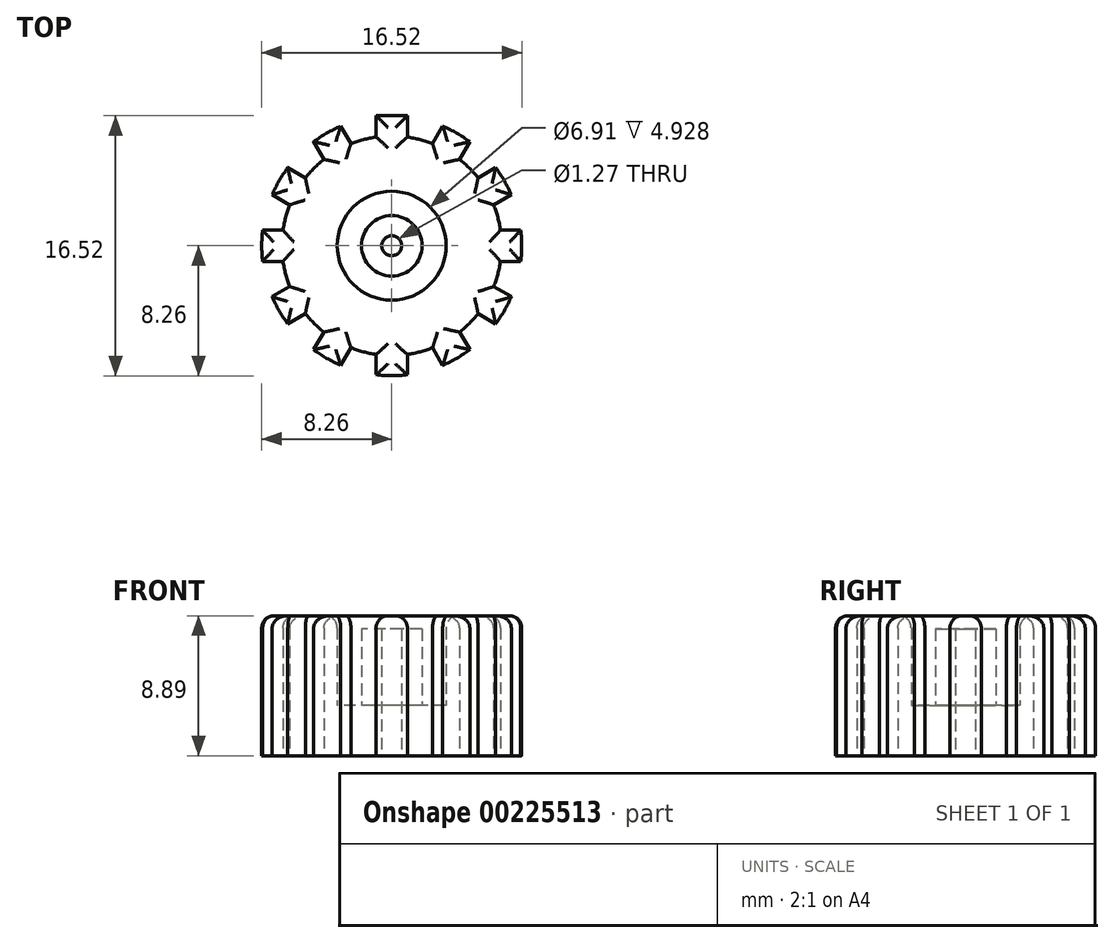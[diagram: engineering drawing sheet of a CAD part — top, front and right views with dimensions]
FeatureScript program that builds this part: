
annotation { "Feature Type Name" : "Feature", "Feature Type Description" : "" }
export const myFeature = defineFeature(function(context is Context, id is Id, definition is map)
    precondition{}
    {
        {
            var Q0;
            Q0=qCreatedBy(makeId("Top.planeOp"),FACE);
            var sketch = newSketch(context, id + "F0", { "sketchPlane" : qUnion([Q0])});
            skArc(sketch, "E0", {"start": v(-1, 8.2) * mm, "mid": v(0, -8.26) * mm, "end": v(1, 8.2) * mm});
            skCircle(sketch, "E1", {"center": v(0, 0) * mm, "radius": 0.64 * mm});
            skCircle(sketch, "E2", {"center": v(0, 0) * mm, "radius": 6.97 * mm});
            skLineSegment(sketch, "E3.top", {"start": v(-1, 8.26) * mm, "end": v(1, 8.26) * mm});
            skLineSegment(sketch, "E3.left", {"start": v(-1, 6.9) * mm, "end": v(-1, 8.26) * mm});
            skLineSegment(sketch, "E3.right", {"start": v(1, 6.9) * mm, "end": v(1, 8.26) * mm});
            skPoint(sketch, "E3.middle", {"position": v(0, 7.58) * mm});
            skLineSegment(sketch, "E4.1.0", {"start": v(-4.99, 6.65) * mm, "end": v(-3.27, 7.65) * mm});
            skLineSegment(sketch, "E4.1.1", {"start": v(-4.31, 5.48) * mm, "end": v(-4.99, 6.65) * mm});
            skLineSegment(sketch, "E4.1.2", {"start": v(-2.6, 6.47) * mm, "end": v(-3.27, 7.65) * mm});
            skLineSegment(sketch, "E4.2.0", {"start": v(-7.65, 3.27) * mm, "end": v(-6.65, 4.99) * mm});
            skLineSegment(sketch, "E4.2.1", {"start": v(-6.47, 2.6) * mm, "end": v(-7.65, 3.27) * mm});
            skLineSegment(sketch, "E4.2.2", {"start": v(-5.48, 4.31) * mm, "end": v(-6.65, 4.99) * mm});
            skLineSegment(sketch, "E4.3.0", {"start": v(-8.26, -1) * mm, "end": v(-8.26, 1) * mm});
            skLineSegment(sketch, "E4.3.1", {"start": v(-6.9, -1) * mm, "end": v(-8.26, -1) * mm});
            skLineSegment(sketch, "E4.3.2", {"start": v(-6.9, 1) * mm, "end": v(-8.26, 1) * mm});
            skLineSegment(sketch, "E4.4.0", {"start": v(-6.65, -4.99) * mm, "end": v(-7.65, -3.27) * mm});
            skLineSegment(sketch, "E4.4.1", {"start": v(-5.48, -4.31) * mm, "end": v(-6.65, -4.99) * mm});
            skLineSegment(sketch, "E4.4.2", {"start": v(-6.47, -2.6) * mm, "end": v(-7.65, -3.27) * mm});
            skLineSegment(sketch, "E4.5.0", {"start": v(-3.27, -7.65) * mm, "end": v(-4.99, -6.65) * mm});
            skLineSegment(sketch, "E4.5.1", {"start": v(-2.6, -6.47) * mm, "end": v(-3.27, -7.65) * mm});
            skLineSegment(sketch, "E4.5.2", {"start": v(-4.31, -5.48) * mm, "end": v(-4.99, -6.65) * mm});
            skLineSegment(sketch, "E4.6.0", {"start": v(1, -8.26) * mm, "end": v(-1, -8.26) * mm});
            skLineSegment(sketch, "E4.6.1", {"start": v(1, -6.9) * mm, "end": v(1, -8.26) * mm});
            skLineSegment(sketch, "E4.6.2", {"start": v(-1, -6.9) * mm, "end": v(-1, -8.26) * mm});
            skLineSegment(sketch, "E4.7.0", {"start": v(4.99, -6.65) * mm, "end": v(3.27, -7.65) * mm});
            skLineSegment(sketch, "E4.7.1", {"start": v(4.31, -5.48) * mm, "end": v(4.99, -6.65) * mm});
            skLineSegment(sketch, "E4.7.2", {"start": v(2.6, -6.47) * mm, "end": v(3.27, -7.65) * mm});
            skLineSegment(sketch, "E4.8.0", {"start": v(7.65, -3.27) * mm, "end": v(6.65, -4.99) * mm});
            skLineSegment(sketch, "E4.8.1", {"start": v(6.47, -2.6) * mm, "end": v(7.65, -3.27) * mm});
            skLineSegment(sketch, "E4.8.2", {"start": v(5.48, -4.31) * mm, "end": v(6.65, -4.99) * mm});
            skLineSegment(sketch, "E4.9.0", {"start": v(8.26, 1) * mm, "end": v(8.26, -1) * mm});
            skLineSegment(sketch, "E4.9.1", {"start": v(6.9, 1) * mm, "end": v(8.26, 1) * mm});
            skLineSegment(sketch, "E4.9.2", {"start": v(6.9, -1) * mm, "end": v(8.26, -1) * mm});
            skLineSegment(sketch, "E4.10.0", {"start": v(6.65, 4.99) * mm, "end": v(7.65, 3.27) * mm});
            skLineSegment(sketch, "E4.10.1", {"start": v(5.48, 4.31) * mm, "end": v(6.65, 4.99) * mm});
            skLineSegment(sketch, "E4.10.2", {"start": v(6.47, 2.6) * mm, "end": v(7.65, 3.27) * mm});
            skLineSegment(sketch, "E4.11.0", {"start": v(3.27, 7.65) * mm, "end": v(4.99, 6.65) * mm});
            skLineSegment(sketch, "E4.11.1", {"start": v(2.6, 6.47) * mm, "end": v(3.27, 7.65) * mm});
            skLineSegment(sketch, "E4.11.2", {"start": v(4.31, 5.48) * mm, "end": v(4.99, 6.65) * mm});
            skCircle(sketch, "E5", {"center": v(0, 0) * mm, "radius": 3.46 * mm});
            skCircle(sketch, "E6", {"center": v(0, 0) * mm, "radius": 1.92 * mm});
            skSolve(sketch);
        }
        {
            var Q0;
            Q0=makeQuery(id+"F0.imprint","IMPRINT",FACE,{"disambiguationData":[TD([[makeQuery(id+"F0.imprint","IMPRINT",EDGE,{"derivedFrom":sQuery(id+"F0.wireOp",EDGE,"E5")}),-1.0]])]});
            var Q1;
            {var subQ1=sQuery(id+"F0.wireOp",EDGE,"E4.1.2");var subQ3=sQuery(id+"F0.wireOp",EDGE,"E0");var subQ4=makeQuery(id+"F0.imprint","INTERSECT",VERTEX,{"derivedFrom":[subQ3,subQ1]});Q1=makeQuery(id+"F0.imprint","IMPRINT",FACE,{"disambiguationData":[TD([[makeQuery(id+"F0.imprint","IMPRINT",EDGE,{"disambiguationData":[TD([[subQ4,-1.0]])],"derivedFrom":subQ3}),1.0]])]});}
            var Q2;
            {var subQ3=sQuery(id+"F0.wireOp",EDGE,"E0");var subQ5=sQuery(id+"F0.wireOp",EDGE,"E4.2.2");var subQ7=makeQuery(id+"F0.imprint","INTERSECT",VERTEX,{"derivedFrom":[subQ3,subQ5]});Q2=makeQuery(id+"F0.imprint","IMPRINT",FACE,{"disambiguationData":[TD([[makeQuery(id+"F0.imprint","IMPRINT",EDGE,{"disambiguationData":[TD([[subQ7,-1.0]])],"derivedFrom":subQ3}),1.0]])]});}
            var Q3;
            {var subQ3=sQuery(id+"F0.wireOp",EDGE,"E0");var subQ5=sQuery(id+"F0.wireOp",EDGE,"E4.3.2");var subQ7=makeQuery(id+"F0.imprint","INTERSECT",VERTEX,{"derivedFrom":[subQ3,subQ5]});Q3=makeQuery(id+"F0.imprint","IMPRINT",FACE,{"disambiguationData":[TD([[makeQuery(id+"F0.imprint","IMPRINT",EDGE,{"disambiguationData":[TD([[subQ7,-1.0]])],"derivedFrom":subQ3}),1.0]])]});}
            var Q4;
            {var subQ1=sQuery(id+"F0.wireOp",EDGE,"E4.4.2");var subQ3=sQuery(id+"F0.wireOp",EDGE,"E0");var subQ4=makeQuery(id+"F0.imprint","INTERSECT",VERTEX,{"derivedFrom":[subQ3,subQ1]});Q4=makeQuery(id+"F0.imprint","IMPRINT",FACE,{"disambiguationData":[TD([[makeQuery(id+"F0.imprint","IMPRINT",EDGE,{"disambiguationData":[TD([[subQ4,-1.0]])],"derivedFrom":subQ3}),1.0]])]});}
            var Q5;
            {var subQ1=sQuery(id+"F0.wireOp",EDGE,"E4.5.2");var subQ3=sQuery(id+"F0.wireOp",EDGE,"E0");var subQ4=makeQuery(id+"F0.imprint","INTERSECT",VERTEX,{"derivedFrom":[subQ3,subQ1]});Q5=makeQuery(id+"F0.imprint","IMPRINT",FACE,{"disambiguationData":[TD([[makeQuery(id+"F0.imprint","IMPRINT",EDGE,{"disambiguationData":[TD([[subQ4,-1.0]])],"derivedFrom":subQ3}),1.0]])]});}
            var Q6;
            {var subQ1=sQuery(id+"F0.wireOp",EDGE,"E4.6.2");var subQ3=sQuery(id+"F0.wireOp",EDGE,"E0");var subQ4=makeQuery(id+"F0.imprint","INTERSECT",VERTEX,{"derivedFrom":[subQ3,subQ1]});Q6=makeQuery(id+"F0.imprint","IMPRINT",FACE,{"disambiguationData":[TD([[makeQuery(id+"F0.imprint","IMPRINT",EDGE,{"disambiguationData":[TD([[subQ4,-1.0]])],"derivedFrom":subQ3}),1.0]])]});}
            var Q7;
            {var subQ3=sQuery(id+"F0.wireOp",EDGE,"E0");var subQ5=sQuery(id+"F0.wireOp",EDGE,"E4.7.2");var subQ7=makeQuery(id+"F0.imprint","INTERSECT",VERTEX,{"derivedFrom":[subQ3,subQ5]});Q7=makeQuery(id+"F0.imprint","IMPRINT",FACE,{"disambiguationData":[TD([[makeQuery(id+"F0.imprint","IMPRINT",EDGE,{"disambiguationData":[TD([[subQ7,-1.0]])],"derivedFrom":subQ3}),1.0]])]});}
            var Q8;
            {var subQ1=sQuery(id+"F0.wireOp",EDGE,"E4.8.2");var subQ3=sQuery(id+"F0.wireOp",EDGE,"E0");var subQ4=makeQuery(id+"F0.imprint","INTERSECT",VERTEX,{"derivedFrom":[subQ3,subQ1]});Q8=makeQuery(id+"F0.imprint","IMPRINT",FACE,{"disambiguationData":[TD([[makeQuery(id+"F0.imprint","IMPRINT",EDGE,{"disambiguationData":[TD([[subQ4,-1.0]])],"derivedFrom":subQ3}),1.0]])]});}
            var Q9;
            {var subQ1=sQuery(id+"F0.wireOp",EDGE,"E4.9.2");var subQ3=sQuery(id+"F0.wireOp",EDGE,"E0");var subQ4=makeQuery(id+"F0.imprint","INTERSECT",VERTEX,{"derivedFrom":[subQ3,subQ1]});Q9=makeQuery(id+"F0.imprint","IMPRINT",FACE,{"disambiguationData":[TD([[makeQuery(id+"F0.imprint","IMPRINT",EDGE,{"disambiguationData":[TD([[subQ4,-1.0]])],"derivedFrom":subQ3}),1.0]])]});}
            var Q10;
            {var subQ1=sQuery(id+"F0.wireOp",EDGE,"E4.10.2");var subQ3=sQuery(id+"F0.wireOp",EDGE,"E0");var subQ4=makeQuery(id+"F0.imprint","INTERSECT",VERTEX,{"derivedFrom":[subQ3,subQ1]});Q10=makeQuery(id+"F0.imprint","IMPRINT",FACE,{"disambiguationData":[TD([[makeQuery(id+"F0.imprint","IMPRINT",EDGE,{"disambiguationData":[TD([[subQ4,-1.0]])],"derivedFrom":subQ3}),1.0]])]});}
            var Q11;
            {var subQ1=sQuery(id+"F0.wireOp",EDGE,"E4.11.2");var subQ3=sQuery(id+"F0.wireOp",EDGE,"E0");var subQ4=makeQuery(id+"F0.imprint","INTERSECT",VERTEX,{"derivedFrom":[subQ3,subQ1]});Q11=makeQuery(id+"F0.imprint","IMPRINT",FACE,{"disambiguationData":[TD([[makeQuery(id+"F0.imprint","IMPRINT",EDGE,{"disambiguationData":[TD([[subQ4,-1.0]])],"derivedFrom":subQ3}),1.0]])]});}
            var Q12;
            {var subQ7=sQuery(id+"F0.wireOp",EDGE,"E3.top");Q12=makeQuery(id+"F0.imprint","IMPRINT",FACE,{"disambiguationData":[TD([[makeQuery(id+"F0.imprint","IMPRINT",EDGE,{"derivedFrom":subQ7}),-1.0]])]});}
            extrude(context, id + "F1", {"entities" : qUnion([Q0, Q1, Q2, Q3, Q4, Q5, Q6, Q7, Q8, Q9, Q10, Q11, Q12]), "depth" : 8.9 * mm});
        }
        {
            var Q0;
            Q0=makeQuery(id+"F0.imprint","IMPRINT",FACE,{"disambiguationData":[TD([[makeQuery(id+"F0.imprint","IMPRINT",EDGE,{"derivedFrom":sQuery(id+"F0.wireOp",EDGE,"E5")}),1.0]])]});
            extrude(context, id + "F2", {"entities" : qUnion([Q0]), "operationType" : NewBodyOperationType.ADD, "depth" : 3.2 * mm});
        }
        {
            var Q0;
            Q0=makeQuery(id+"F0.imprint","IMPRINT",FACE,{"disambiguationData":[TD([[makeQuery(id+"F0.imprint","IMPRINT",EDGE,{"derivedFrom":sQuery(id+"F0.wireOp",EDGE,"E1")}),-1.0]])]});
            extrude(context, id + "F3", {"entities" : qUnion([Q0]), "operationType" : NewBodyOperationType.ADD, "depth" : 8.05 * mm});
        }
        {
            var Q0;
            Q0=makeQuery(id+"F1.opExtrude","CAP_FACE",FACE,{"disambiguationData":[OSD([sQuery(id+"F0.wireOp",EDGE,"E0"),sQuery(id+"F0.wireOp",EDGE,"E3.top"),sQuery(id+"F0.wireOp",EDGE,"E3.left"),sQuery(id+"F0.wireOp",EDGE,"E3.right"),sQuery(id+"F0.wireOp",EDGE,"E4.1.1"),sQuery(id+"F0.wireOp",EDGE,"E4.1.2"),sQuery(id+"F0.wireOp",EDGE,"E4.2.1"),sQuery(id+"F0.wireOp",EDGE,"E4.2.2"),sQuery(id+"F0.wireOp",EDGE,"E4.3.1"),sQuery(id+"F0.wireOp",EDGE,"E4.3.2"),sQuery(id+"F0.wireOp",EDGE,"E4.4.1"),sQuery(id+"F0.wireOp",EDGE,"E4.4.2"),sQuery(id+"F0.wireOp",EDGE,"E4.5.1"),sQuery(id+"F0.wireOp",EDGE,"E4.5.2"),sQuery(id+"F0.wireOp",EDGE,"E4.6.1"),sQuery(id+"F0.wireOp",EDGE,"E4.6.2"),sQuery(id+"F0.wireOp",EDGE,"E4.7.1"),sQuery(id+"F0.wireOp",EDGE,"E4.7.2"),sQuery(id+"F0.wireOp",EDGE,"E4.8.1"),sQuery(id+"F0.wireOp",EDGE,"E4.8.2"),sQuery(id+"F0.wireOp",EDGE,"E4.9.1"),sQuery(id+"F0.wireOp",EDGE,"E4.9.2"),sQuery(id+"F0.wireOp",EDGE,"E4.10.1"),sQuery(id+"F0.wireOp",EDGE,"E4.10.2"),sQuery(id+"F0.wireOp",EDGE,"E4.11.1"),sQuery(id+"F0.wireOp",EDGE,"E4.11.2"),sQuery(id+"F0.wireOp",EDGE,"E2"),sQuery(id+"F0.wireOp",EDGE,"E5")])],"isStart":false});
            fillet(context, id + "F4", {"entities" : qUnion([Q0]), "radius" : 0.76 * mm, "tangentPropagation" : true, "allowEdgeOverflow" : false});
        }
    });
